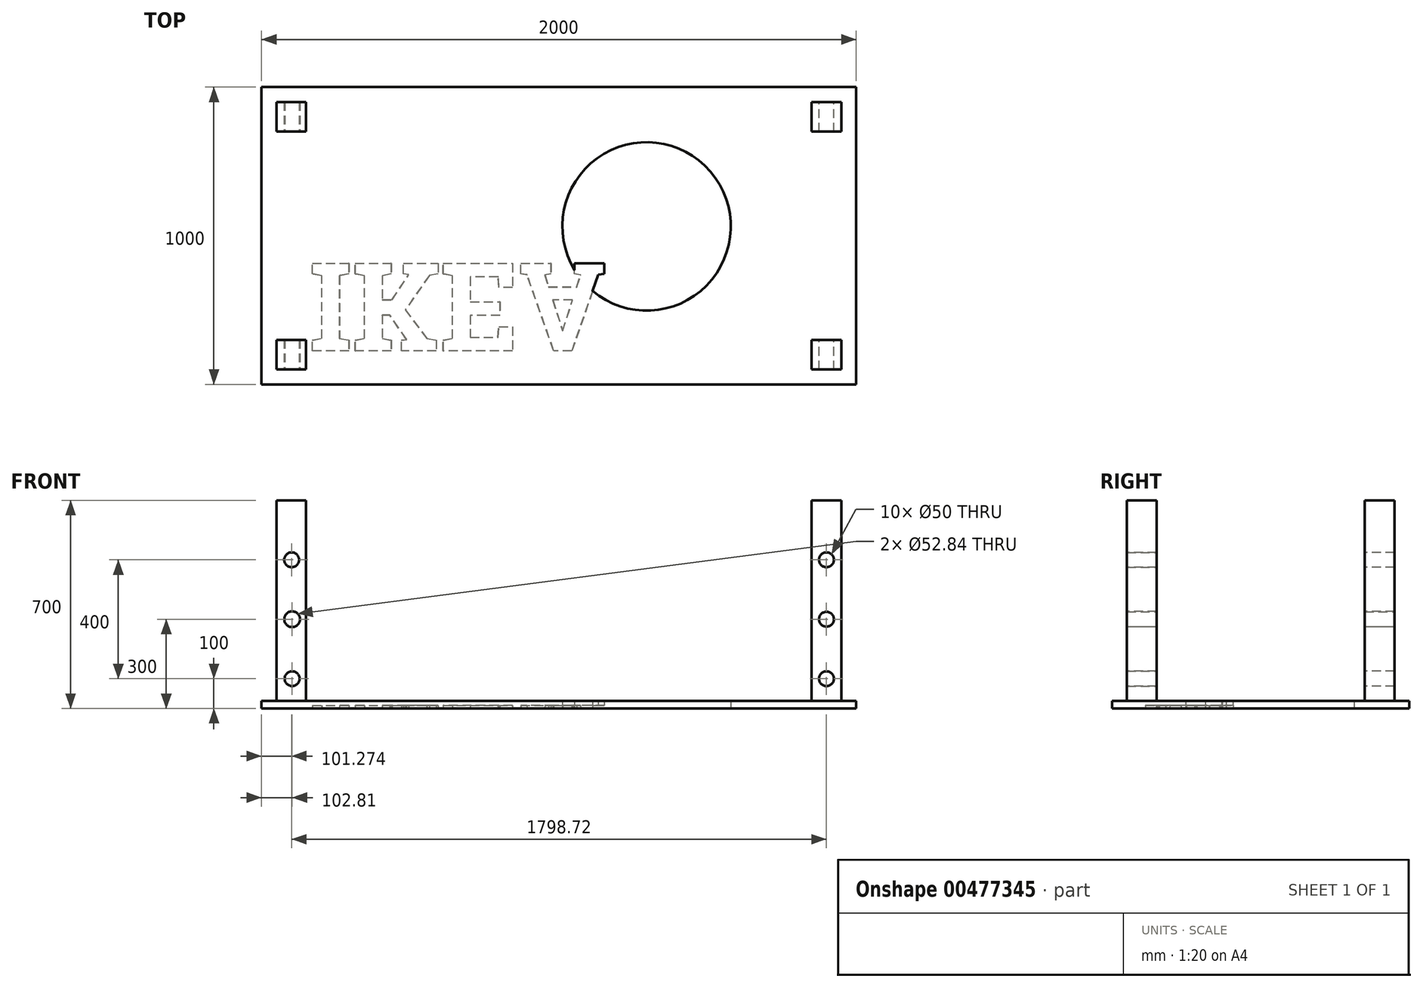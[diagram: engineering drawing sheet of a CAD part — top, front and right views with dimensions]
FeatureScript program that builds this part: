
annotation { "Feature Type Name" : "Feature", "Feature Type Description" : "" }
export const myFeature = defineFeature(function(context is Context, id is Id, definition is map)
    precondition{}
    {
        {
            var Q0;
            Q0=qCreatedBy(makeId("Top.planeOp"),FACE);
            var sketch = newSketch(context, id + "F0", { "sketchPlane" : qUnion([Q0])});
            skLineSegment(sketch, "E0.bottom", {"start": v(-1015.07, 208.85) * mm, "end": v(984.93, 208.85) * mm});
            skLineSegment(sketch, "E0.top", {"start": v(-1015.07, -791.15) * mm, "end": v(984.93, -791.15) * mm});
            skLineSegment(sketch, "E0.left", {"start": v(-1015.07, 208.85) * mm, "end": v(-1015.07, -791.15) * mm});
            skLineSegment(sketch, "E0.right", {"start": v(984.93, 208.85) * mm, "end": v(984.93, -791.15) * mm});
            skSolve(sketch);
        }
        {
            var Q0;
            Q0 = qSketchRegion(id + "F0", true);
            extrude(context, id + "F1", {"entities" : qUnion([Q0]), "depth" : 25 * mm});
        }
        {
            var Q0;
            Q0=qCreatedBy(makeId("Top.planeOp"),FACE);
            var sketch = newSketch(context, id + "F2", { "sketchPlane" : qUnion([Q0])});
            skLineSegment(sketch, "E1.bottom", {"start": v(-965.07, 158.85) * mm, "end": v(-865.07, 158.85) * mm});
            skLineSegment(sketch, "E1.top", {"start": v(-965.07, 58.85) * mm, "end": v(-865.07, 58.85) * mm});
            skLineSegment(sketch, "E1.left", {"start": v(-965.07, 158.85) * mm, "end": v(-965.07, 58.85) * mm});
            skLineSegment(sketch, "E1.right", {"start": v(-865.07, 158.85) * mm, "end": v(-865.07, 58.85) * mm});
            skLineSegment(sketch, "E2.bottom", {"start": v(-965.07, -641.15) * mm, "end": v(-865.07, -641.15) * mm});
            skLineSegment(sketch, "E2.top", {"start": v(-965.07, -741.15) * mm, "end": v(-865.07, -741.15) * mm});
            skLineSegment(sketch, "E2.left", {"start": v(-965.07, -641.15) * mm, "end": v(-965.07, -741.15) * mm});
            skLineSegment(sketch, "E2.right", {"start": v(-865.07, -641.15) * mm, "end": v(-865.07, -741.15) * mm});
            skLineSegment(sketch, "E3.bottom", {"start": v(834.93, 158.85) * mm, "end": v(934.93, 158.85) * mm});
            skLineSegment(sketch, "E3.top", {"start": v(834.93, 58.85) * mm, "end": v(934.93, 58.85) * mm});
            skLineSegment(sketch, "E3.left", {"start": v(834.93, 158.85) * mm, "end": v(834.93, 58.85) * mm});
            skLineSegment(sketch, "E3.right", {"start": v(934.93, 158.85) * mm, "end": v(934.93, 58.85) * mm});
            skLineSegment(sketch, "E4.bottom", {"start": v(834.93, -641.15) * mm, "end": v(934.93, -641.15) * mm});
            skLineSegment(sketch, "E4.top", {"start": v(834.93, -741.15) * mm, "end": v(934.93, -741.15) * mm});
            skLineSegment(sketch, "E4.left", {"start": v(834.93, -641.15) * mm, "end": v(834.93, -741.15) * mm});
            skLineSegment(sketch, "E4.right", {"start": v(934.93, -641.15) * mm, "end": v(934.93, -741.15) * mm});
            skSolve(sketch);
        }
        {
            var Q0;
            Q0 = qSketchRegion(id + "F2", true);
            extrude(context, id + "F3", {"entities" : qUnion([Q0]), "operationType" : NewBodyOperationType.ADD, "depth" : 700 * mm});
        }
        {
            var Q0;
            Q0=makeQuery(id+"F3.opExtrude","SWEPT_FACE",FACE,{"disambiguationData":[OSD([sQuery(id+"F2.wireOp",EDGE,"E2.top")])]});
            var sketch = newSketch(context, id + "F4", { "sketchPlane" : qUnion([Q0])});
            skCircle(sketch, "E5", {"center": v(-913.8, 500) * mm, "radius": 25 * mm});
            skCircle(sketch, "E6", {"center": v(-912.26, 300) * mm, "radius": 26.42 * mm});
            skCircle(sketch, "E7", {"center": v(-912.26, 100) * mm, "radius": 25 * mm});
            skSolve(sketch);
        }
        {
            var Q0;
            Q0=makeQuery(id+"F3.opExtrude","SWEPT_FACE",FACE,{"disambiguationData":[OSD([sQuery(id+"F2.wireOp",EDGE,"E3.bottom")])]});
            var sketch = newSketch(context, id + "F5", { "sketchPlane" : qUnion([Q0])});
            skCircle(sketch, "E8", {"center": v(-884.93, 500) * mm, "radius": 25 * mm});
            skCircle(sketch, "E9", {"center": v(-884.93, 300) * mm, "radius": 25 * mm});
            skCircle(sketch, "E10", {"center": v(-884.93, 100) * mm, "radius": 25 * mm});
            skSolve(sketch);
        }
        {
            var Q0;
            Q0 = qSketchRegion(id + "F4", true);
            extrude(context, id + "F6", {"entities" : qUnion([Q0]), "operationType" : NewBodyOperationType.REMOVE, "endBound" : BoundingType.THROUGH_ALL, "oppositeDirection" : true, "depth" : 25 * mm});
        }
        {
            var Q0;
            Q0 = qSketchRegion(id + "F5", true);
            extrude(context, id + "F7", {"entities" : qUnion([Q0]), "operationType" : NewBodyOperationType.REMOVE, "endBound" : BoundingType.THROUGH_ALL, "oppositeDirection" : true, "depth" : 25 * mm});
        }
        {
            var Q0;
            Q0=makeQuery(id+"F1.opExtrude","CAP_FACE",FACE,{"disambiguationData":[OSD([sQuery(id+"F0.wireOp",EDGE,"E0.bottom"),sQuery(id+"F0.wireOp",EDGE,"E0.top"),sQuery(id+"F0.wireOp",EDGE,"E0.left"),sQuery(id+"F0.wireOp",EDGE,"E0.right")])],"isStart":true});
            var sketch = newSketch(context, id + "F8", { "sketchPlane" : qUnion([Q0])});
            skText(sketch, "E11", { "text": "IKEA", "fontName": "RobotoSlab-Bold.ttf"});
            const initialGuessF8  = {"E11": [-0.8548, 0.3842, 1, 0, 0.29783]};
            skSetInitialGuess(sketch, initialGuessF8);
            skSolve(sketch);
        }
        {
            var Q0;
            Q0 = qSketchRegion(id + "F8", true);
            extrude(context, id + "F9", {"entities" : qUnion([Q0]), "operationType" : NewBodyOperationType.REMOVE, "oppositeDirection" : true, "depth" : 10 * mm, "hasDraft" : true, "draftAngle" : 3 * degree});
        }
        {
            var Q0;
            {var subQ0=sQuery(id+"F0.wireOp",EDGE,"E0.right");var subQ1=sQuery(id+"F0.wireOp",EDGE,"E0.bottom");var subQ2=sQuery(id+"F0.wireOp",EDGE,"E0.top");var subQ3=sQuery(id+"F0.wireOp",EDGE,"E0.left");Q0=makeQuery(id+"F9.boolean.opBoolean","SPLIT",FACE,{"disambiguationData":[TD([makeQuery(id+"F1.opExtrude","SWEPT_FACE",FACE,{"disambiguationData":[OSD([subQ1])]})])],"derivedFrom":makeQuery(id+"F1.opExtrude","CAP_FACE",FACE,{"disambiguationData":[OSD([subQ1,subQ2,subQ3,subQ0])],"isStart":true})});}
            var sketch = newSketch(context, id + "F10", { "sketchPlane" : qUnion([Q0])});
            skCircle(sketch, "E12", {"center": v(279.96, 259.92) * mm, "radius": 283.15 * mm});
            skSolve(sketch);
        }
        {
            var Q0;
            {var subQ1=makeQuery(id+"F9.boolean.opBoolean","COPY",EDGE,{"derivedFrom":makeQuery(id+"F9.opExtrude","CAP_EDGE",EDGE,{"disambiguationData":[OSD([sQuery(id+"F8.wireOp",EDGE,"E11.sketch_text.stroke-66")])],"isStart":true})});Q0=makeQuery(id+"F10.imprint","IMPRINT",FACE,{"disambiguationData":[TD([[makeQuery(id+"F10.imprint","IMPRINT",EDGE,{"derivedFrom":subQ1}),1.0]])]});}
            extrude(context, id + "F11", {"entities" : qUnion([Q0]), "operationType" : NewBodyOperationType.REMOVE, "oppositeDirection" : true, "depth" : 25 * mm});
        }
    });
